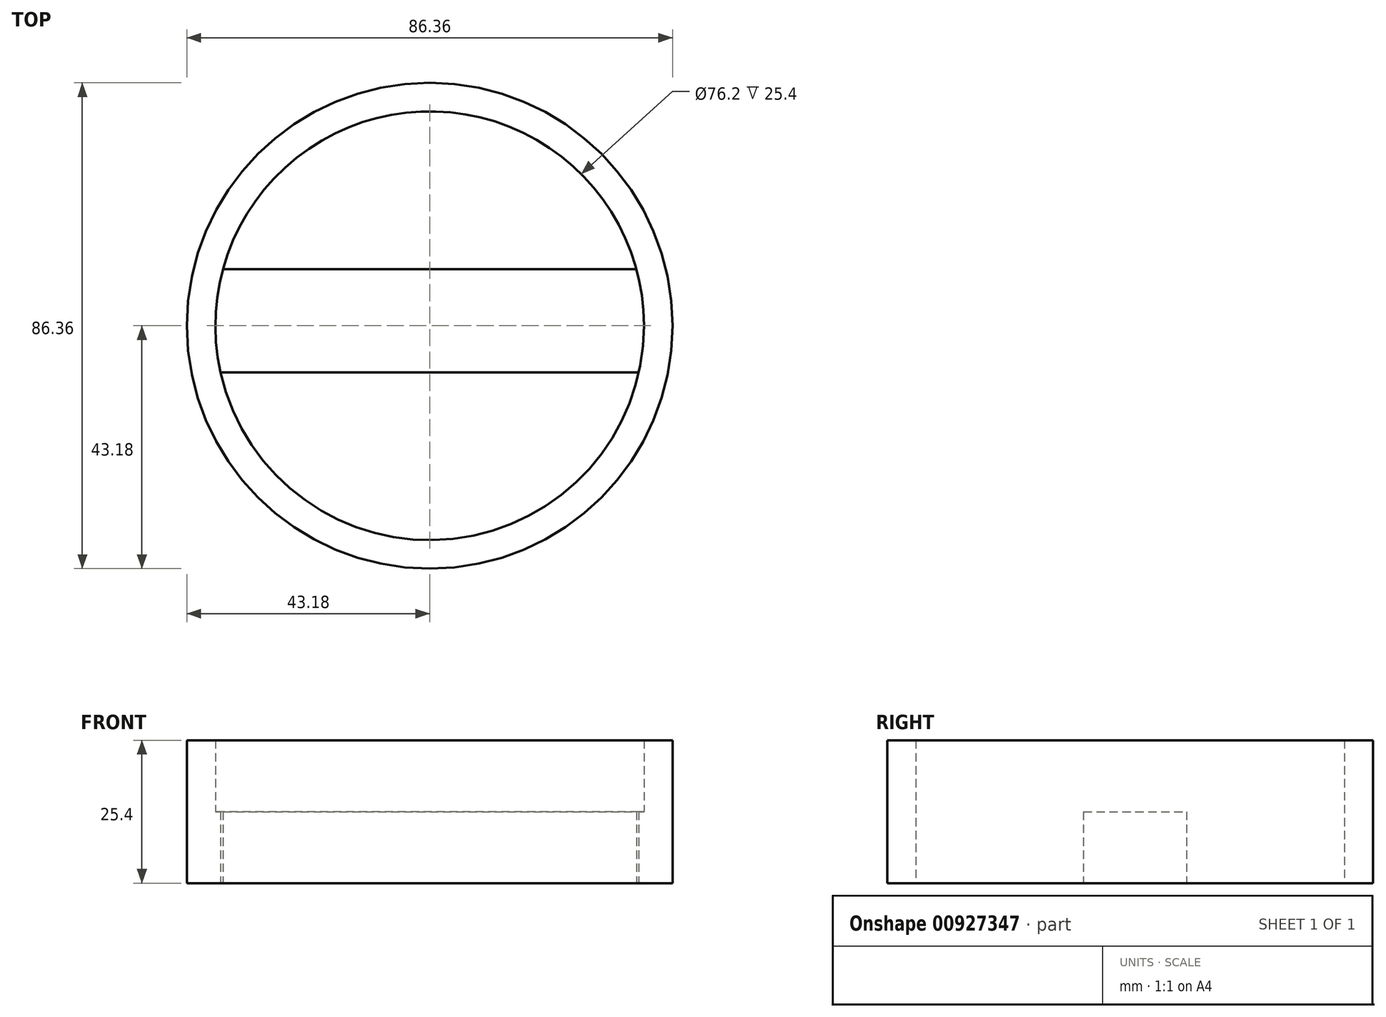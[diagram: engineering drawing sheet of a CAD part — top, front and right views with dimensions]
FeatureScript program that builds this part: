
annotation { "Feature Type Name" : "Feature", "Feature Type Description" : "" }
export const myFeature = defineFeature(function(context is Context, id is Id, definition is map)
    precondition{}
    {
        {
            var Q0;
            Q0=qCreatedBy(makeId("Top.planeOp"),FACE);
            var sketch = newSketch(context, id + "F0", { "sketchPlane" : qUnion([Q0])});
            skCircle(sketch, "E0", {"center": v(0, 0) * mm, "radius": 38.1 * mm});
            skEllipse(sketch, "E1", {"center": v(-30.05, 34.94) * mm, "majorRadius": 22.23 * mm, "minorRadius": 17.88 * mm, "majorAxis": v(0.74, 0.67)});
            skLineSegment(sketch, "E2", {"start": v(0, -51.2) * mm, "end": v(0, 70.22) * mm, "construction": true});
            skEllipse(sketch, "E3.MirrorC", {"center": v(30.05, 34.94) * mm, "majorRadius": 22.23 * mm, "minorRadius": 17.88 * mm, "majorAxis": v(-0.74, 0.67)});
            skLineSegment(sketch, "E4", {"start": v(37.19, -8.3) * mm, "end": v(-37.19, -8.3) * mm});
            skFitSpline(sketch, "E5.0", {"points": [v(-8.2, 51.34) * mm, v(-9.69, 53.2) * mm, v(-11.4, 54.89) * mm, v(-13.9, 56.82) * mm, v(-16.74, 58.3) * mm, v(-19.8, 59.27) * mm, v(-22.98, 59.9) * mm, v(-27.07, 60.08) * mm, v(-31.17, 59.47) * mm, v(-34.42, 58.53) * mm, v(-37.59, 57.3) * mm, v(-40.6, 55.7) * mm, v(-43.41, 53.72) * mm, v(-45.41, 52.06) * mm, v(-47.27, 50.25) * mm, v(-49.54, 47.67) * mm, v(-51.47, 44.85) * mm, v(-53.03, 41.84) * mm, v(-54.32, 38.7) * mm, v(-55.37, 34.7) * mm, v(-55.64, 30.62) * mm, v(-55.35, 27.38) * mm, v(-54.7, 24.23) * mm, v(-53.55, 21.25) * mm, v(-51.9, 18.55) * mm, v(-50.42, 16.67) * mm, v(-48.72, 15) * mm, v(-46.2, 13.06) * mm, v(-43.37, 11.6) * mm, v(-40.3, 10.62) * mm, v(-37.12, 9.98) * mm, v(-33.04, 9.8) * mm, v(-28.93, 10.42) * mm, v(-25.68, 11.36) * mm, v(-22.52, 12.58) * mm, v(-19.5, 14.2) * mm, v(-16.7, 16.17) * mm, v(-14.7, 17.82) * mm, v(-12.83, 19.63) * mm, v(-10.57, 22.21) * mm, v(-8.64, 25.03) * mm, v(-7.08, 28.05) * mm, v(-5.8, 31.18) * mm, v(-4.74, 35.2) * mm, v(-4.47, 39.27) * mm, v(-4.76, 42.5) * mm, v(-5.4, 45.65) * mm, v(-6.55, 48.63) * mm, v(-8.2, 51.34) * mm, v(-9.69, 53.2) * mm, v(-11.4, 54.89) * mm, v(-8.2, 51.34) * mm]});
            skFitSpline(sketch, "E6.0", {"points": [v(11.4, 54.89) * mm, v(9.69, 53.2) * mm, v(8.2, 51.34) * mm, v(6.55, 48.63) * mm, v(5.4, 45.65) * mm, v(4.76, 42.5) * mm, v(4.47, 39.27) * mm, v(4.74, 35.2) * mm, v(5.8, 31.18) * mm, v(7.08, 28.05) * mm, v(8.64, 25.03) * mm, v(10.57, 22.21) * mm, v(12.83, 19.63) * mm, v(14.7, 17.82) * mm, v(16.7, 16.17) * mm, v(19.5, 14.2) * mm, v(22.52, 12.58) * mm, v(25.68, 11.36) * mm, v(28.93, 10.42) * mm, v(33.04, 9.8) * mm, v(37.12, 9.98) * mm, v(40.3, 10.62) * mm, v(43.37, 11.6) * mm, v(46.2, 13.06) * mm, v(48.72, 15) * mm, v(50.42, 16.67) * mm, v(51.9, 18.55) * mm, v(53.55, 21.25) * mm, v(54.7, 24.23) * mm, v(55.35, 27.38) * mm, v(55.64, 30.62) * mm, v(55.37, 34.7) * mm, v(54.32, 38.7) * mm, v(53.03, 41.84) * mm, v(51.47, 44.85) * mm, v(49.54, 47.67) * mm, v(47.27, 50.25) * mm, v(45.41, 52.06) * mm, v(43.41, 53.72) * mm, v(40.6, 55.7) * mm, v(37.59, 57.3) * mm, v(34.42, 58.53) * mm, v(31.17, 59.47) * mm, v(27.07, 60.08) * mm, v(22.98, 59.9) * mm, v(19.8, 59.27) * mm, v(16.74, 58.3) * mm, v(13.9, 56.82) * mm, v(11.4, 54.89) * mm, v(9.69, 53.2) * mm, v(8.2, 51.34) * mm, v(11.4, 54.89) * mm]});
            skCircle(sketch, "E7.0", {"center": v(0, 0) * mm, "radius": 43.18 * mm});
            skLineSegment(sketch, "E8", {"start": v(-36.75, 10.04) * mm, "end": v(36.75, 10.04) * mm});
            skLineSegment(sketch, "E9", {"start": v(36.75, 10.04) * mm, "end": v(37.19, -8.3) * mm});
            skLineSegment(sketch, "E10", {"start": v(-36.75, 10.04) * mm, "end": v(-37.19, -8.3) * mm});
            skSolve(sketch);
        }
        {
            var Q0;
            {var subQ1=sQuery(id+"F0.wireOp",EDGE,"E0");var subQ3=sQuery(id+"F0.wireOp",EDGE,"E3.MirrorC");var subQ4=makeQuery(id+"F0.imprint","INTERSECT",VERTEX,{"disambiguationData":[OD(0.0)],"derivedFrom":[subQ1,subQ3]});Q0=makeQuery(id+"F0.imprint","IMPRINT",FACE,{"disambiguationData":[TD([[makeQuery(id+"F0.imprint","IMPRINT",EDGE,{"disambiguationData":[TD([[subQ4,-1.0]])],"derivedFrom":subQ3}),-1.0]])]});}
            var Q1;
            {var subQ0=sQuery(id+"F0.wireOp",EDGE,"E7.0");var subQ1=sQuery(id+"F0.wireOp",EDGE,"E3.MirrorC");var subQ2=makeQuery(id+"F0.imprint","INTERSECT",VERTEX,{"disambiguationData":[OD(0.0)],"derivedFrom":[subQ1,subQ0]});Q1=makeQuery(id+"F0.imprint","IMPRINT",FACE,{"disambiguationData":[TD([[makeQuery(id+"F0.imprint","IMPRINT",EDGE,{"disambiguationData":[TD([[subQ2,1.0]])],"derivedFrom":subQ1}),-1.0]])]});}
            var Q2;
            {var subQ0=sQuery(id+"F0.wireOp",EDGE,"E7.0");var subQ1=sQuery(id+"F0.wireOp",EDGE,"E1");var subQ2=makeQuery(id+"F0.imprint","INTERSECT",VERTEX,{"disambiguationData":[OD(0.0)],"derivedFrom":[subQ1,subQ0]});Q2=makeQuery(id+"F0.imprint","IMPRINT",FACE,{"disambiguationData":[TD([[makeQuery(id+"F0.imprint","IMPRINT",EDGE,{"disambiguationData":[TD([[subQ2,1.0]])],"derivedFrom":subQ1}),-1.0]])]});}
            var Q3;
            {var subQ0=sQuery(id+"F0.wireOp",EDGE,"E5.0");var subQ1=sQuery(id+"F0.wireOp",EDGE,"E0");var subQ2=makeQuery(id+"F0.imprint","INTERSECT",VERTEX,{"derivedFrom":[subQ1,subQ0]});Q3=makeQuery(id+"F0.imprint","IMPRINT",FACE,{"disambiguationData":[TD([[makeQuery(id+"F0.imprint","IMPRINT",EDGE,{"disambiguationData":[TD([[subQ2,-1.0]])],"derivedFrom":subQ1}),-1.0]])]});}
            var Q4;
            {var subQ1=sQuery(id+"F0.wireOp",EDGE,"E0");var subQ3=sQuery(id+"F0.wireOp",EDGE,"E1");var subQ4=makeQuery(id+"F0.imprint","INTERSECT",VERTEX,{"disambiguationData":[OD(1.0)],"derivedFrom":[subQ1,subQ3]});Q4=makeQuery(id+"F0.imprint","IMPRINT",FACE,{"disambiguationData":[TD([[makeQuery(id+"F0.imprint","IMPRINT",EDGE,{"disambiguationData":[TD([[subQ4,1.0]])],"derivedFrom":subQ3}),-1.0]])]});}
            var Q5;
            {var subQ2=sQuery(id+"F0.wireOp",EDGE,"E5.0");var subQ5=sQuery(id+"F0.wireOp",EDGE,"E7.0");var subQ6=makeQuery(id+"F0.imprint","INTERSECT",VERTEX,{"disambiguationData":[OD(0.0)],"derivedFrom":[subQ2,subQ5]});Q5=makeQuery(id+"F0.imprint","IMPRINT",FACE,{"disambiguationData":[TD([[makeQuery(id+"F0.imprint","IMPRINT",EDGE,{"disambiguationData":[TD([[subQ6,-1.0]])],"derivedFrom":subQ5}),1.0]])]});}
            var Q6;
            {var subQ0=sQuery(id+"F0.wireOp",EDGE,"E6.0");var subQ1=sQuery(id+"F0.wireOp",EDGE,"E0");var subQ2=makeQuery(id+"F0.imprint","INTERSECT",VERTEX,{"derivedFrom":[subQ1,subQ0]});Q6=makeQuery(id+"F0.imprint","IMPRINT",FACE,{"disambiguationData":[TD([[makeQuery(id+"F0.imprint","IMPRINT",EDGE,{"disambiguationData":[TD([[subQ2,-1.0]])],"derivedFrom":subQ1}),-1.0]])]});}
            var Q7;
            {var subQ0=sQuery(id+"F0.wireOp",EDGE,"E3.MirrorC");var subQ1=sQuery(id+"F0.wireOp",EDGE,"E0");var subQ2=makeQuery(id+"F0.imprint","INTERSECT",VERTEX,{"disambiguationData":[OD(1.0)],"derivedFrom":[subQ1,subQ0]});Q7=makeQuery(id+"F0.imprint","IMPRINT",FACE,{"disambiguationData":[TD([[makeQuery(id+"F0.imprint","IMPRINT",EDGE,{"disambiguationData":[TD([[subQ2,-1.0]])],"derivedFrom":subQ1}),-1.0]])]});}
            extrude(context, id + "F1", {"entities" : qUnion([Q0, Q1, Q2, Q3, Q4, Q5, Q6, Q7]), "depth" : 25.4 * mm, "offsetDistance" : 25.4 * mm});
        }
        {
            var Q0;
            {var subQ0=sQuery(id+"F0.wireOp",EDGE,"E10");Q0=makeQuery(id+"F0.imprint","IMPRINT",FACE,{"disambiguationData":[TD([[makeQuery(id+"F0.imprint","IMPRINT",EDGE,{"derivedFrom":subQ0}),-1.0]])]});}
            var Q1;
            {var subQ0=sQuery(id+"F0.wireOp",EDGE,"E9");Q1=makeQuery(id+"F0.imprint","IMPRINT",FACE,{"disambiguationData":[TD([[makeQuery(id+"F0.imprint","IMPRINT",EDGE,{"derivedFrom":subQ0}),1.0]])]});}
            var Q2;
            Q2=makeQuery(id+"F0.imprint","IMPRINT",FACE,{"disambiguationData":[TD([[makeQuery(id+"F0.imprint","IMPRINT",EDGE,{"derivedFrom":sQuery(id+"F0.wireOp",EDGE,"E4")}),-1.0]])]});
            extrude(context, id + "F2", {"entities" : qUnion([Q0, Q1, Q2]), "operationType" : NewBodyOperationType.ADD, "depth" : 12.7 * mm, "offsetDistance" : 25.4 * mm});
        }
    });
